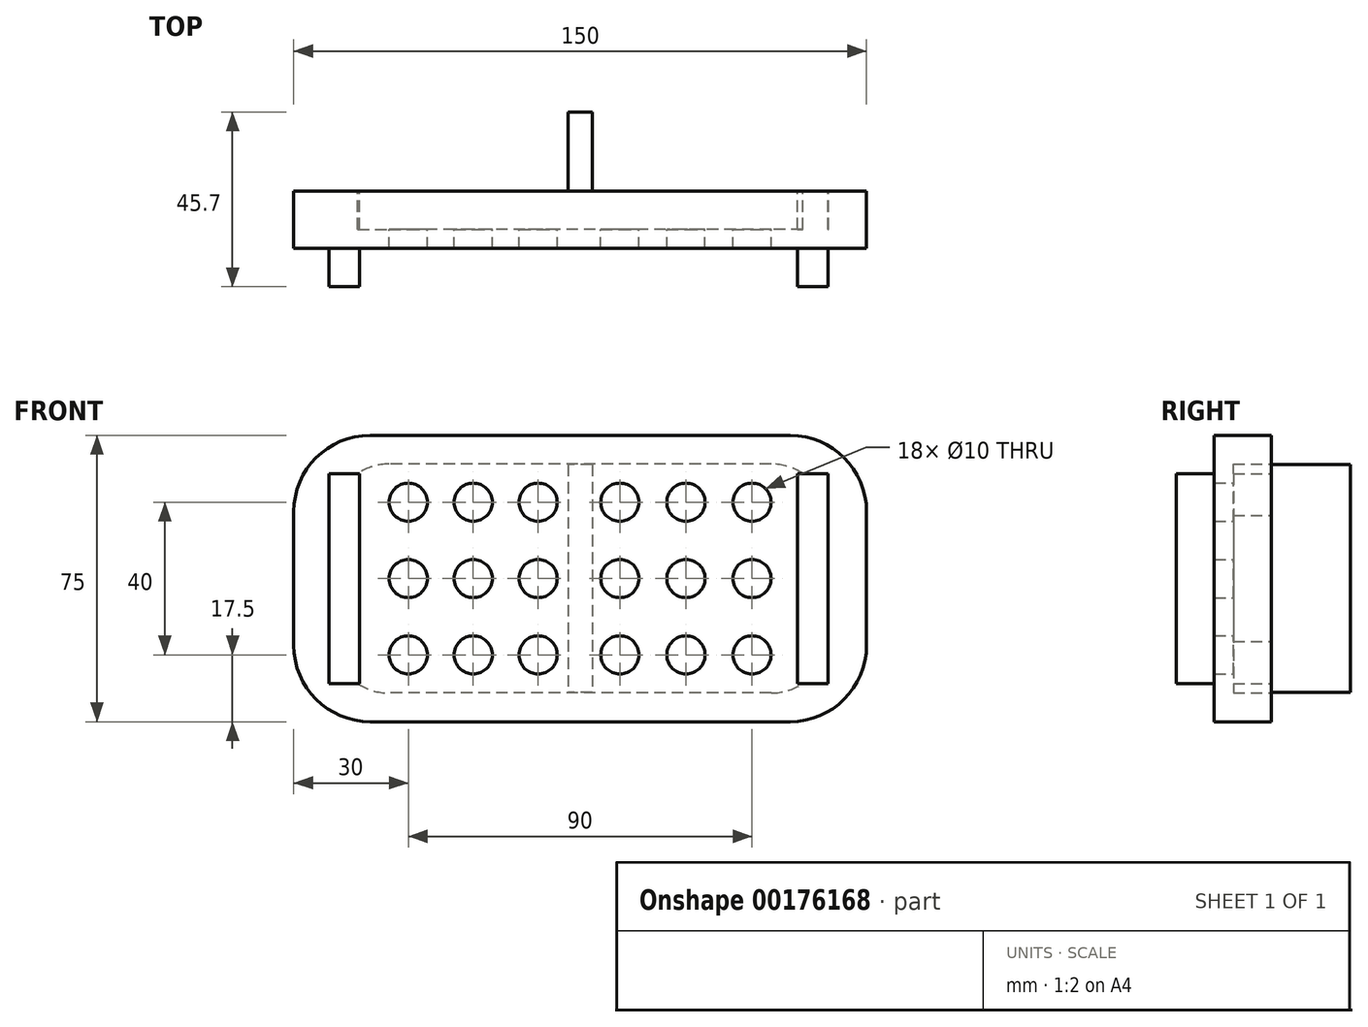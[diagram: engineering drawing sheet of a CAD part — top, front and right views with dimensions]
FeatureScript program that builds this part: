
annotation { "Feature Type Name" : "Feature", "Feature Type Description" : "" }
export const myFeature = defineFeature(function(context is Context, id is Id, definition is map)
    precondition{}
    {
        {
            var Q0;
            Q0=qCreatedBy(makeId("Front.planeOp"),FACE);
            var sketch = newSketch(context, id + "F0", { "sketchPlane" : qUnion([Q0])});
            skLineSegment(sketch, "E0.bottom", {"start": v(-55, 37.5) * mm, "end": v(55, 37.5) * mm});
            skLineSegment(sketch, "E0.top", {"start": v(-55, -37.5) * mm, "end": v(55, -37.5) * mm});
            skLineSegment(sketch, "E0.left", {"start": v(-75, 17.5) * mm, "end": v(-75, -17.5) * mm});
            skLineSegment(sketch, "E0.right", {"start": v(75, 17.5) * mm, "end": v(75, -17.5) * mm});
            skPoint(sketch, "E0.middle", {"position": v(0, 0) * mm});
            skPoint(sketch, "E1.visualSharp", {"position": v(-75, 37.5) * mm});
            skArc(sketch, "E1.filletArc", {"start": v(-55, 37.5) * mm, "mid": v(-69.14, 31.64) * mm, "end": v(-75, 17.5) * mm});
            skPoint(sketch, "E2.visualSharp", {"position": v(75, 37.5) * mm});
            skArc(sketch, "E2.filletArc", {"start": v(75, 17.5) * mm, "mid": v(69.14, 31.64) * mm, "end": v(55, 37.5) * mm});
            skPoint(sketch, "E3.visualSharp", {"position": v(75, -37.5) * mm});
            skArc(sketch, "E3.filletArc", {"start": v(55, -37.5) * mm, "mid": v(69.14, -31.64) * mm, "end": v(75, -17.5) * mm});
            skPoint(sketch, "E4.visualSharp", {"position": v(-75, -37.5) * mm});
            skArc(sketch, "E4.filletArc", {"start": v(-75, -17.5) * mm, "mid": v(-69.14, -31.64) * mm, "end": v(-55, -37.5) * mm});
            skSolve(sketch);
        }
        {
            var Q0;
            Q0=makeQuery(id+"F0.imprint","IMPRINT",FACE,{"disambiguationData":[TD([[makeQuery(id+"F0.imprint","IMPRINT",EDGE,{"derivedFrom":sQuery(id+"F0.wireOp",EDGE,"E0.bottom")}),-1.0]])]});
            extrude(context, id + "F1", {"entities" : qUnion([Q0]), "depth" : 15 * mm});
        }
        {
            var Q0;
            Q0=qCreatedBy(makeId("Front.planeOp"),FACE);
            var sketch = newSketch(context, id + "F2", { "sketchPlane" : qUnion([Q0])});
            skLineSegment(sketch, "E5.bottom", {"start": v(50, 30) * mm, "end": v(-50, 30) * mm});
            skLineSegment(sketch, "E5.top", {"start": v(50, -30) * mm, "end": v(-50, -30) * mm});
            skLineSegment(sketch, "E5.left", {"start": v(65, 15) * mm, "end": v(65, -15) * mm});
            skLineSegment(sketch, "E5.right", {"start": v(-65, 15) * mm, "end": v(-65, -15) * mm});
            skPoint(sketch, "E5.middle", {"position": v(0, 0) * mm});
            skPoint(sketch, "E6.visualSharp", {"position": v(65, 30) * mm});
            skArc(sketch, "E6.filletArc", {"start": v(65, 15) * mm, "mid": v(60.6, 25.6) * mm, "end": v(50, 30) * mm});
            skPoint(sketch, "E7.visualSharp", {"position": v(-65, 30) * mm});
            skArc(sketch, "E7.filletArc", {"start": v(-50, 30) * mm, "mid": v(-60.6, 25.6) * mm, "end": v(-65, 15) * mm});
            skPoint(sketch, "E8.visualSharp", {"position": v(-65, -30) * mm});
            skArc(sketch, "E8.filletArc", {"start": v(-65, -15) * mm, "mid": v(-60.6, -25.6) * mm, "end": v(-50, -30) * mm});
            skPoint(sketch, "E9.visualSharp", {"position": v(65, -30) * mm});
            skArc(sketch, "E9.filletArc", {"start": v(50, -30) * mm, "mid": v(60.6, -25.6) * mm, "end": v(65, -15) * mm});
            skSolve(sketch);
        }
        {
            var Q0;
            Q0 = qSketchRegion(id + "F2", true);
            extrude(context, id + "F3", {"entities" : qUnion([Q0]), "operationType" : NewBodyOperationType.REMOVE, "depth" : 10 * mm});
        }
        {
            var Q0;
            Q0=qCreatedBy(makeId("Front.planeOp"),FACE);
            var sketch = newSketch(context, id + "F4", { "sketchPlane" : qUnion([Q0])});
            skLineSegment(sketch, "E10.bottom", {"start": v(3.14, 29.87) * mm, "end": v(-3.14, 29.87) * mm});
            skLineSegment(sketch, "E10.top", {"start": v(3.14, -29.87) * mm, "end": v(-3.14, -29.87) * mm});
            skLineSegment(sketch, "E10.left", {"start": v(3.14, 29.87) * mm, "end": v(3.14, -29.87) * mm});
            skLineSegment(sketch, "E10.right", {"start": v(-3.14, 29.87) * mm, "end": v(-3.14, -29.87) * mm});
            skPoint(sketch, "E10.middle", {"position": v(0, 0) * mm});
            skSolve(sketch);
        }
        {
            var Q0;
            Q0 = qSketchRegion(id + "F4", true);
            extrude(context, id + "F5", {"entities" : qUnion([Q0]), "oppositeDirection" : true, "depth" : 20.7 * mm});
        }
        {
            var Q0;
            Q0=qCreatedBy(makeId("Front.planeOp"),FACE);
            var sketch = newSketch(context, id + "F6", { "sketchPlane" : qUnion([Q0])});
            skPoint(sketch, "E11.middle", {"position": v(0, 0) * mm});
            skCircle(sketch, "E12", {"center": v(45, -20) * mm, "radius": 5 * mm});
            skCircle(sketch, "E13", {"center": v(45, 0) * mm, "radius": 5 * mm});
            skCircle(sketch, "E14.1.0.0", {"center": v(27.7, 20) * mm, "radius": 5 * mm});
            skCircle(sketch, "E14.2.0.0", {"center": v(10.4, 20) * mm, "radius": 5 * mm});
            skCircle(sketch, "E15.1.0.0", {"center": v(27.7, 0) * mm, "radius": 5 * mm});
            skCircle(sketch, "E15.2.0.0", {"center": v(10.4, 0) * mm, "radius": 5 * mm});
            skCircle(sketch, "E16.1.0.0", {"center": v(27.7, -20) * mm, "radius": 5 * mm});
            skCircle(sketch, "E16.2.0.0", {"center": v(10.4, -20) * mm, "radius": 5 * mm});
            skCircle(sketch, "E17", {"center": v(-45, 20) * mm, "radius": 5 * mm});
            skCircle(sketch, "E18.1.0.0", {"center": v(-28, 20) * mm, "radius": 5 * mm});
            skCircle(sketch, "E18.2.0.0", {"center": v(-11, 20) * mm, "radius": 5 * mm});
            skCircle(sketch, "E19", {"center": v(-45, -20) * mm, "radius": 5 * mm});
            skCircle(sketch, "E20.1.0.0", {"center": v(-28, -20) * mm, "radius": 5 * mm});
            skCircle(sketch, "E20.2.0.0", {"center": v(-11, -20) * mm, "radius": 5 * mm});
            skCircle(sketch, "E21", {"center": v(-45, 0) * mm, "radius": 5 * mm});
            skCircle(sketch, "E22.1.0.0", {"center": v(-28, 0) * mm, "radius": 5 * mm});
            skCircle(sketch, "E22.2.0.0", {"center": v(-11, 0) * mm, "radius": 5 * mm});
            skLineSegment(sketch, "E23.trimOffspring", {"start": v(32.7, 0) * mm, "end": v(27.7, 0) * mm, "construction": true});
            skPoint(sketch, "E24.center.orphan", {"position": v(45, 20) * mm});
            skCircle(sketch, "E25", {"center": v(45, 20) * mm, "radius": 5 * mm});
            skSolve(sketch);
        }
        {
            var Q0;
            Q0 = qSketchRegion(id + "F6", true);
            extrude(context, id + "F7", {"entities" : qUnion([Q0]), "operationType" : NewBodyOperationType.REMOVE, "endBound" : BoundingType.THROUGH_ALL, "depth" : 25 * mm});
        }
        {
            var Q0;
            Q0=qCreatedBy(makeId("Front.planeOp"),FACE);
            var sketch = newSketch(context, id + "F8", { "sketchPlane" : qUnion([Q0])});
            skLineSegment(sketch, "E26.bottom", {"start": v(-65.77, 27.5) * mm, "end": v(-57.77, 27.5) * mm});
            skLineSegment(sketch, "E26.top", {"start": v(-65.77, -27.5) * mm, "end": v(-57.77, -27.5) * mm});
            skLineSegment(sketch, "E26.left", {"start": v(-65.77, 27.5) * mm, "end": v(-65.77, -27.5) * mm});
            skLineSegment(sketch, "E26.right", {"start": v(-57.77, 27.5) * mm, "end": v(-57.77, -27.5) * mm});
            skPoint(sketch, "E26.middle", {"position": v(-61.77, 0) * mm});
            skLineSegment(sketch, "E27.bottom", {"start": v(64.92, -27.5) * mm, "end": v(56.92, -27.5) * mm});
            skLineSegment(sketch, "E27.top", {"start": v(64.92, 27.5) * mm, "end": v(56.92, 27.5) * mm});
            skLineSegment(sketch, "E27.left", {"start": v(64.92, -27.5) * mm, "end": v(64.92, 27.5) * mm});
            skLineSegment(sketch, "E27.right", {"start": v(56.92, -27.5) * mm, "end": v(56.92, 27.5) * mm});
            skPoint(sketch, "E27.middle", {"position": v(60.92, 0) * mm});
            skSolve(sketch);
        }
        {
            var Q0;
            Q0 = qSketchRegion(id + "F8", true);
            extrude(context, id + "F9", {"entities" : qUnion([Q0]), "operationType" : NewBodyOperationType.ADD, "depth" : 25 * mm});
        }
    });
